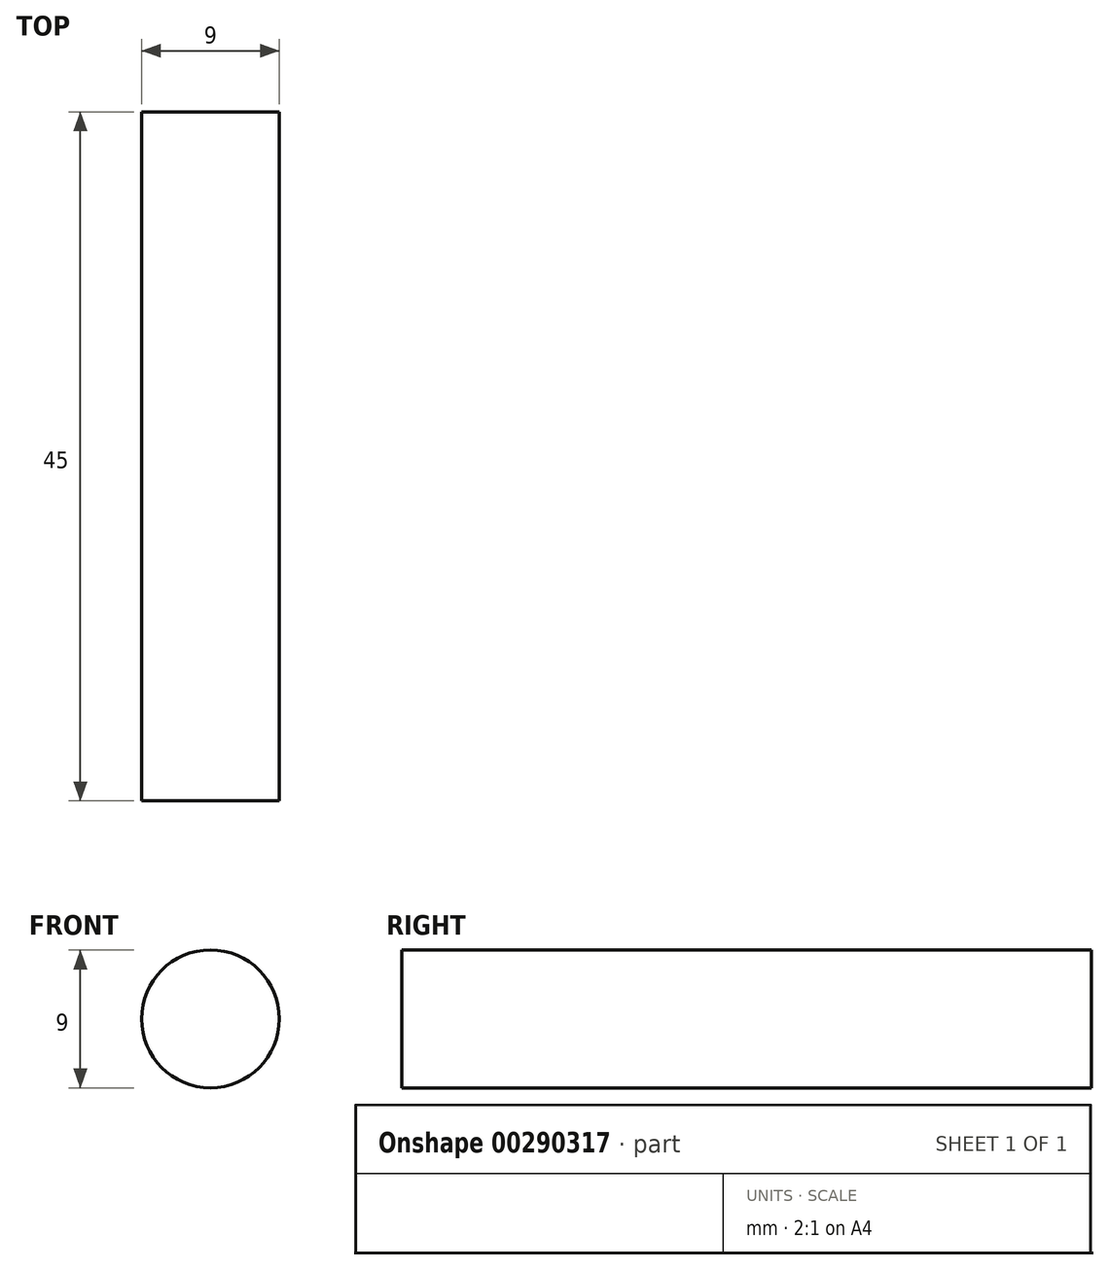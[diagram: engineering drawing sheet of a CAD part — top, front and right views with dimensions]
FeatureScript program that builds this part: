
annotation { "Feature Type Name" : "Feature", "Feature Type Description" : "" }
export const myFeature = defineFeature(function(context is Context, id is Id, definition is map)
    precondition{}
    {
        {
            var Q0;
            Q0=qCreatedBy(makeId("Front.planeOp"),FACE);
            var sketch = newSketch(context, id + "F0", { "sketchPlane" : qUnion([Q0])});
            skCircle(sketch, "E0", {"center": v(0, 0) * mm, "radius": 4.5 * mm});
            skSolve(sketch);
        }
        {
            var Q0;
            Q0 = qSketchRegion(id + "F0", true);
            extrude(context, id + "F1", {"entities" : qUnion([Q0]), "endBound" : BoundingType.SYMMETRIC, "depth" : 45 * mm});
        }
    });
